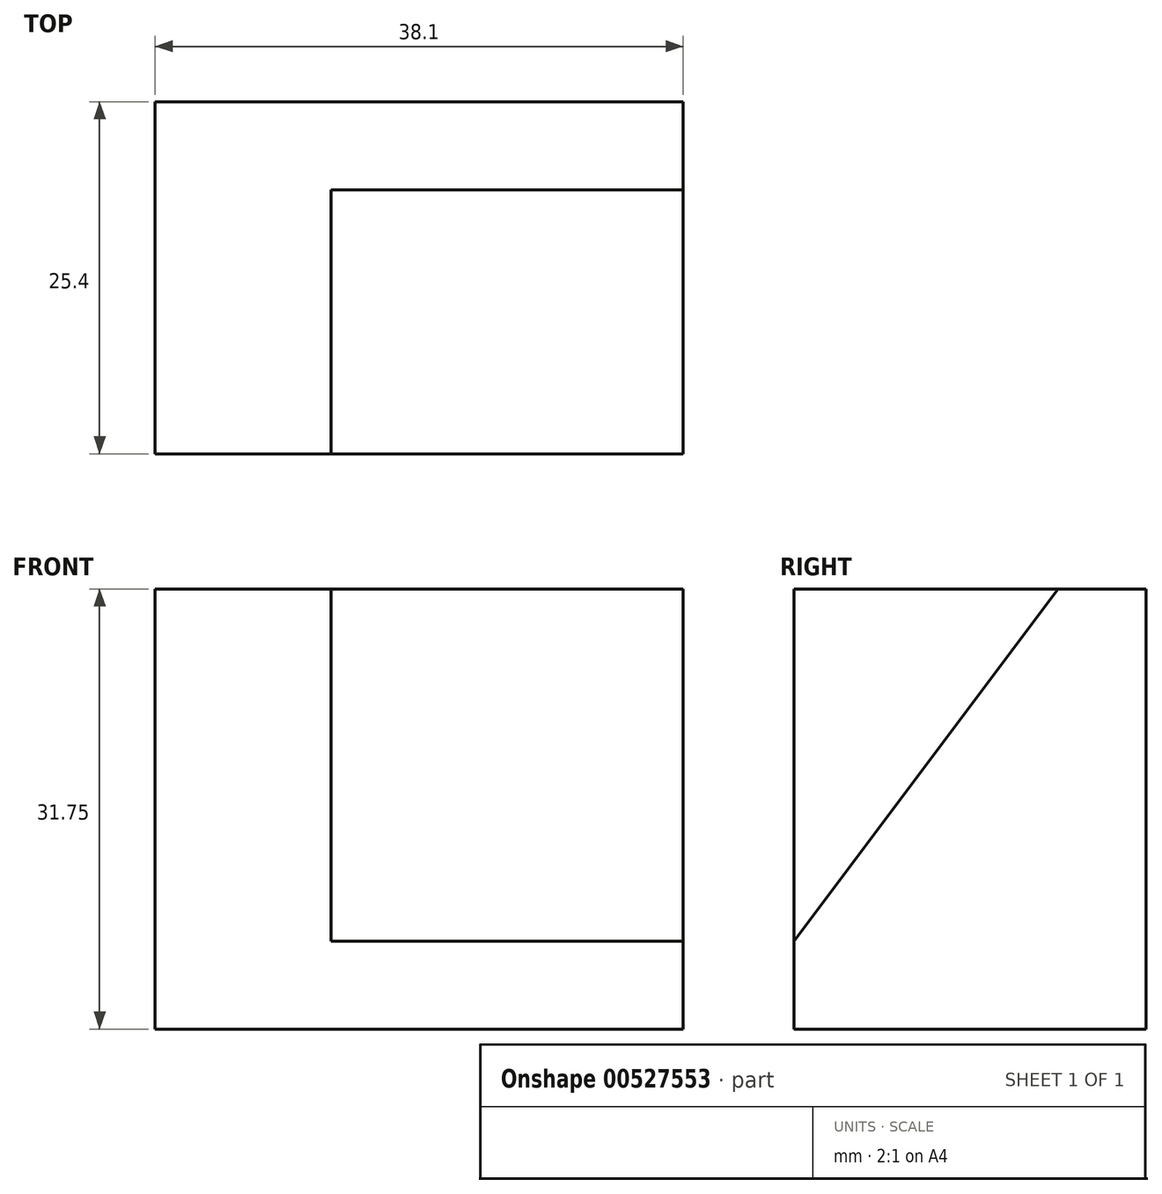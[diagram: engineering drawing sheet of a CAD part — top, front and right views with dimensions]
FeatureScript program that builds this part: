
annotation { "Feature Type Name" : "Feature", "Feature Type Description" : "" }
export const myFeature = defineFeature(function(context is Context, id is Id, definition is map)
    precondition{}
    {
        {
            var Q0;
            Q0=qCreatedBy(makeId("Top.planeOp"),FACE);
            var sketch = newSketch(context, id + "F0", { "sketchPlane" : qUnion([Q0])});
            skLineSegment(sketch, "E0", {"start": v(0, 0) * mm, "end": v(0, 25.4) * mm});
            skLineSegment(sketch, "E1", {"start": v(0, 25.4) * mm, "end": v(38.1, 25.4) * mm});
            skLineSegment(sketch, "E2", {"start": v(38.1, 25.4) * mm, "end": v(38.1, 0) * mm});
            skLineSegment(sketch, "E3", {"start": v(38.1, 0) * mm, "end": v(0, 0) * mm});
            skSolve(sketch);
        }
        {
            var Q0;
            Q0=makeQuery(id+"F0.imprint","IMPRINT",FACE,{"disambiguationData":[TD([[makeQuery(id+"F0.imprint","IMPRINT",EDGE,{"derivedFrom":sQuery(id+"F0.wireOp",EDGE,"E0")}),-1.0]])]});
            extrude(context, id + "F1", {"entities" : qUnion([Q0]), "depth" : 31.75 * mm, "offsetDistance" : 25.4 * mm});
        }
        {
            var Q0;
            Q0=makeQuery(id+"F1.opExtrude","SWEPT_FACE",FACE,{"disambiguationData":[OSD([sQuery(id+"F0.wireOp",EDGE,"E2")])]});
            var sketch = newSketch(context, id + "F2", { "sketchPlane" : qUnion([Q0])});
            skLineSegment(sketch, "E4", {"start": v(19.05, 31.75) * mm, "end": v(0, 6.35) * mm});
            skSolve(sketch);
        }
        {
            var Q0;
            {var subQ0=sQuery(id+"F2.wireOp",EDGE,"E4");Q0=makeQuery(id+"F2.imprint","IMPRINT",FACE,{"disambiguationData":[TD([[makeQuery(id+"F2.imprint","IMPRINT",EDGE,{"derivedFrom":subQ0}),-1.0]])]});}
            extrude(context, id + "F3", {"entities" : qUnion([Q0]), "operationType" : NewBodyOperationType.REMOVE, "oppositeDirection" : true, "depth" : 25.4 * mm, "offsetDistance" : 25.4 * mm});
        }
    });
